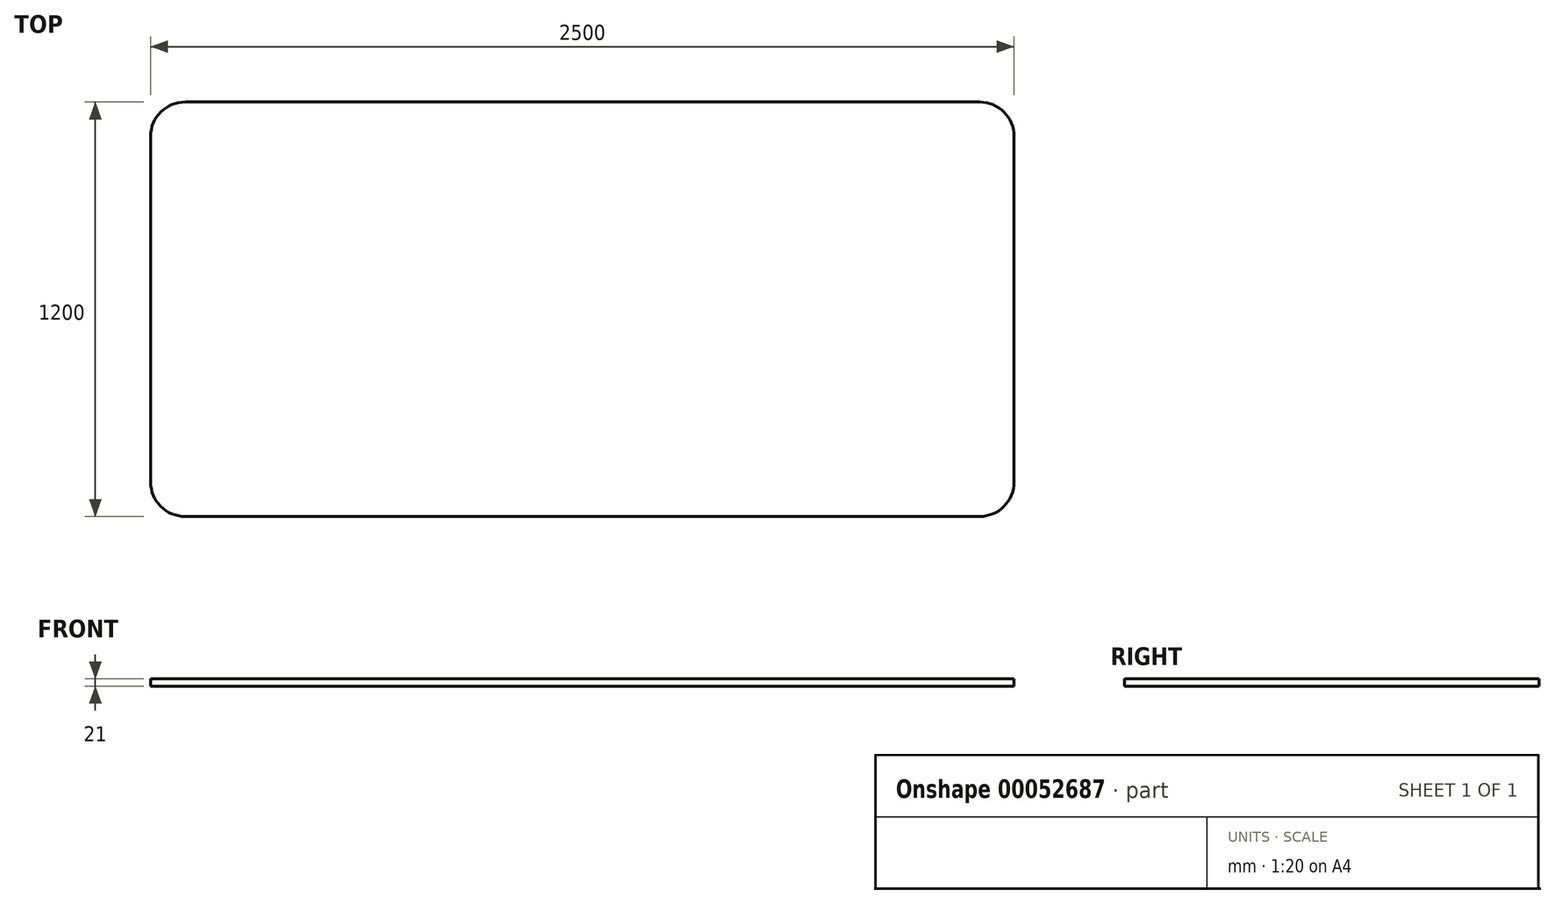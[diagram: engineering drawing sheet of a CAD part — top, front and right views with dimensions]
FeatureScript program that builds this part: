
annotation { "Feature Type Name" : "Feature", "Feature Type Description" : "" }
export const myFeature = defineFeature(function(context is Context, id is Id, definition is map)
    precondition{}
    {
        {
            var Q0;
            Q0=qCreatedBy(makeId("Top.planeOp"),FACE);
            var sketch = newSketch(context, id + "F0", { "sketchPlane" : qUnion([Q0])});
            skLineSegment(sketch, "E0.bottom", {"start": v(0, 0) * mm, "end": v(2500, 0) * mm});
            skLineSegment(sketch, "E0.top", {"start": v(0, 1200) * mm, "end": v(2500, 1200) * mm});
            skLineSegment(sketch, "E0.left", {"start": v(0, 0) * mm, "end": v(0, 1200) * mm});
            skLineSegment(sketch, "E0.right", {"start": v(2500, 0) * mm, "end": v(2500, 1200) * mm});
            skSolve(sketch);
        }
        {
            var Q0;
            Q0 = qSketchRegion(id + "F0", true);
            extrude(context, id + "F1", {"entities" : qUnion([Q0]), "depth" : 21 * mm});
        }
        {
            var Q0;
            Q0=makeQuery(id+"F1.opExtrude","SWEPT_EDGE",EDGE,{"disambiguationData":[OSD([sQuery(id+"F0.wireOp",EDGE,"E0.bottom"),sQuery(id+"F0.wireOp",EDGE,"E0.left")])]});
            var Q1;
            Q1=makeQuery(id+"F1.opExtrude","SWEPT_EDGE",EDGE,{"disambiguationData":[OSD([sQuery(id+"F0.wireOp",EDGE,"E0.bottom"),sQuery(id+"F0.wireOp",EDGE,"E0.right")])]});
            var Q2;
            Q2=makeQuery(id+"F1.opExtrude","SWEPT_EDGE",EDGE,{"disambiguationData":[OSD([sQuery(id+"F0.wireOp",EDGE,"E0.top"),sQuery(id+"F0.wireOp",EDGE,"E0.right")])]});
            var Q3;
            Q3=makeQuery(id+"F1.opExtrude","SWEPT_EDGE",EDGE,{"disambiguationData":[OSD([sQuery(id+"F0.wireOp",EDGE,"E0.top"),sQuery(id+"F0.wireOp",EDGE,"E0.left")])]});
            fillet(context, id + "F2", {"entities" : qUnion([Q0, Q1, Q2, Q3]), "radius" : 100 * mm, "tangentPropagation" : true, "allowEdgeOverflow" : false});
        }
    });
